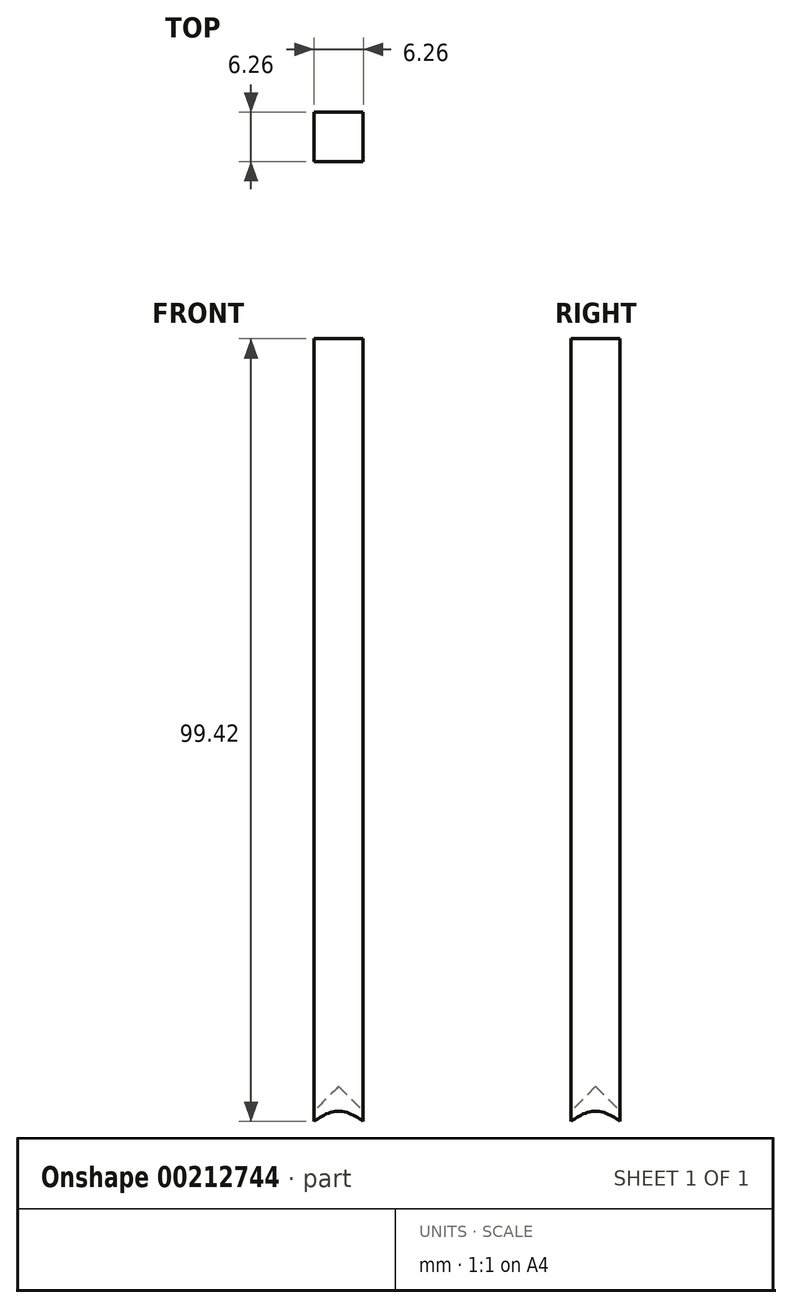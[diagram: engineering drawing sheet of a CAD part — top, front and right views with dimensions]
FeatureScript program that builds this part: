
annotation { "Feature Type Name" : "Feature", "Feature Type Description" : "" }
export const myFeature = defineFeature(function(context is Context, id is Id, definition is map)
    precondition{}
    {
        {
            var Q0;
            Q0=qCreatedBy(makeId("Top.planeOp"),FACE);
            var sketch = newSketch(context, id + "F0", { "sketchPlane" : qUnion([Q0])});
            skLineSegment(sketch, "E0.bottom", {"start": v(3.13, 3.12) * mm, "end": v(-3.12, 3.12) * mm});
            skLineSegment(sketch, "E0.top", {"start": v(3.12, -3.12) * mm, "end": v(-3.13, -3.12) * mm});
            skLineSegment(sketch, "E0.left", {"start": v(3.13, 3.12) * mm, "end": v(3.12, -3.12) * mm});
            skLineSegment(sketch, "E0.right", {"start": v(-3.13, 3.12) * mm, "end": v(-3.13, -3.12) * mm});
            skPoint(sketch, "E0.middle", {"position": v(0, 0) * mm});
            skSolve(sketch);
        }
        {
            var Q0;
            Q0=makeQuery(id+"F0.imprint","IMPRINT",FACE,{"disambiguationData":[TD([[makeQuery(id+"F0.imprint","IMPRINT",EDGE,{"derivedFrom":sQuery(id+"F0.wireOp",EDGE,"E0.bottom")}),1.0]])]});
            extrude(context, id + "F1", {"entities" : qUnion([Q0]), "depth" : 100 * mm});
        }
        {
            var Q0;
            Q0=qCreatedBy(makeId("Front.planeOp"),FACE);
            var sketch = newSketch(context, id + "F2", { "sketchPlane" : qUnion([Q0])});
            skLineSegment(sketch, "E1", {"start": v(0, 5) * mm, "end": v(0, -20) * mm});
            skLineSegment(sketch, "E2", {"start": v(0, -20) * mm, "end": v(25, -20) * mm});
            skLineSegment(sketch, "E3", {"start": v(25, -20) * mm, "end": v(0, 5) * mm});
            skSolve(sketch);
        }
        {
            var Q0;
            Q0=makeQuery(id+"F2.imprint","IMPRINT",FACE,{"disambiguationData":[TD([[makeQuery(id+"F2.imprint","IMPRINT",EDGE,{"derivedFrom":sQuery(id+"F2.wireOp",EDGE,"E1")}),1.0]])]});
            var Q1;
            Q1=sQuery(id+"F2.wireOp",EDGE,"E1");
            revolve(context, id + "F3", {"operationType" : NewBodyOperationType.REMOVE, "entities" : qUnion([Q0]), "axis" : qUnion([Q1]), "revolveType" : RevolveType.FULL, "oppositeDirection" : true});
        }
    });
